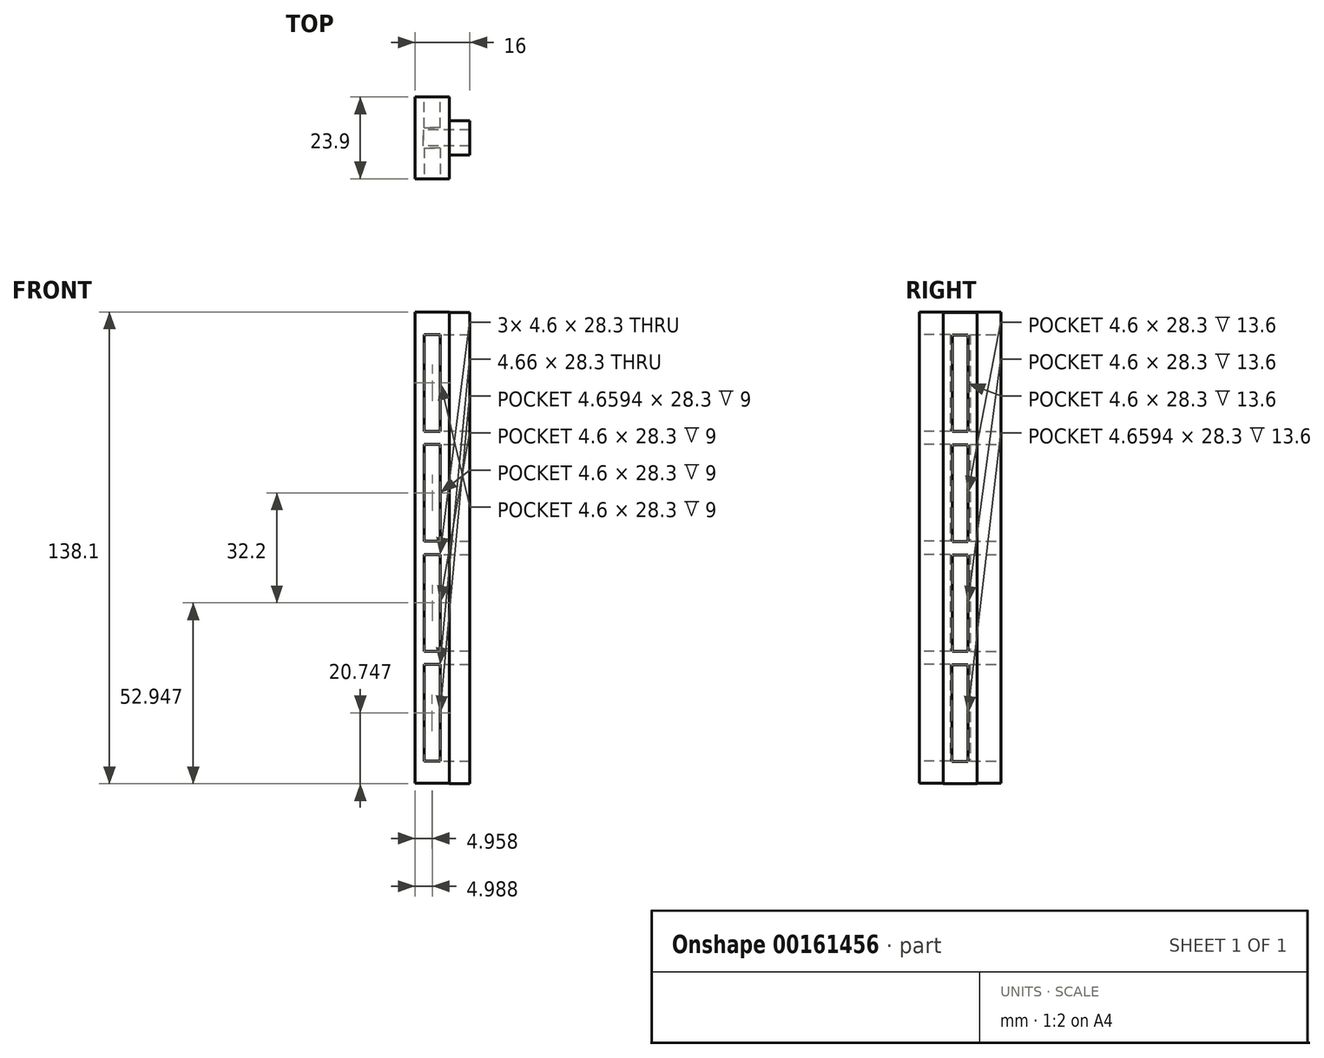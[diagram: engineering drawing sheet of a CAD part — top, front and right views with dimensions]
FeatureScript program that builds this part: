
annotation { "Feature Type Name" : "Feature", "Feature Type Description" : "" }
export const myFeature = defineFeature(function(context is Context, id is Id, definition is map)
    precondition{}
    {
        {
            var Q0;
            Q0=qCreatedBy(makeId("Front.planeOp"),FACE);
            var sketch = newSketch(context, id + "F0", { "sketchPlane" : qUnion([Q0])});
            skLineSegment(sketch, "E0.bottom", {"start": v(-30.25, 56.68) * mm, "end": v(-20.25, 56.68) * mm});
            skLineSegment(sketch, "E0.top", {"start": v(-30.25, -81.32) * mm, "end": v(-20.25, -81.32) * mm});
            skLineSegment(sketch, "E0.left", {"start": v(-30.25, 56.68) * mm, "end": v(-30.25, -81.32) * mm});
            skLineSegment(sketch, "E0.right", {"start": v(-20.25, 56.68) * mm, "end": v(-20.25, -81.32) * mm});
            skLineSegment(sketch, "E1.bottom", {"start": v(-27.56, 50.08) * mm, "end": v(-22.96, 50.08) * mm});
            skLineSegment(sketch, "E1.top", {"start": v(-27.56, 21.78) * mm, "end": v(-22.96, 21.78) * mm});
            skLineSegment(sketch, "E1.left", {"start": v(-27.56, 50.08) * mm, "end": v(-27.56, 21.78) * mm});
            skLineSegment(sketch, "E1.right", {"start": v(-22.96, 50.08) * mm, "end": v(-22.96, 21.78) * mm});
            skLineSegment(sketch, "E2", {"start": v(-26.53, 56.68) * mm, "end": v(-26.53, 50.08) * mm, "construction": true});
            skLineSegment(sketch, "E3", {"start": v(-27.56, 45.9) * mm, "end": v(-30.25, 45.9) * mm, "construction": true});
            skLineSegment(sketch, "E4", {"start": v(-22.96, 46.31) * mm, "end": v(-20.25, 46.31) * mm, "construction": true});
            skLineSegment(sketch, "E5", {"start": v(-25.26, 21.78) * mm, "end": v(-25.26, 17.88) * mm, "construction": true});
            skLineSegment(sketch, "E6", {"start": v(-27.56, 21.78) * mm, "end": v(-27.56, 17.88) * mm, "construction": true});
            skLineSegment(sketch, "E7", {"start": v(-22.96, 21.78) * mm, "end": v(-22.96, 17.88) * mm, "construction": true});
            skLineSegment(sketch, "E8.bottom", {"start": v(-27.56, 17.88) * mm, "end": v(-22.96, 17.88) * mm});
            skLineSegment(sketch, "E8.top", {"start": v(-27.56, -10.42) * mm, "end": v(-22.96, -10.42) * mm});
            skLineSegment(sketch, "E8.left", {"start": v(-27.56, 17.88) * mm, "end": v(-27.56, -10.42) * mm});
            skLineSegment(sketch, "E8.right", {"start": v(-22.96, 17.88) * mm, "end": v(-22.96, -10.42) * mm});
            skLineSegment(sketch, "E9", {"start": v(-22.96, -10.42) * mm, "end": v(-22.96, -14.32) * mm, "construction": true});
            skLineSegment(sketch, "E10", {"start": v(-27.56, -10.42) * mm, "end": v(-27.56, -14.32) * mm, "construction": true});
            skLineSegment(sketch, "E11.bottom", {"start": v(-27.56, -14.32) * mm, "end": v(-22.96, -14.32) * mm});
            skLineSegment(sketch, "E11.top", {"start": v(-27.56, -42.62) * mm, "end": v(-22.96, -42.62) * mm});
            skLineSegment(sketch, "E11.left", {"start": v(-27.56, -14.32) * mm, "end": v(-27.56, -42.62) * mm});
            skLineSegment(sketch, "E11.right", {"start": v(-22.96, -14.32) * mm, "end": v(-22.96, -42.62) * mm});
            skLineSegment(sketch, "E12", {"start": v(-27.56, -41.18) * mm, "end": v(-27.56, -42.62) * mm});
            skLineSegment(sketch, "E13", {"start": v(-22.96, -42.62) * mm, "end": v(-22.96, -46.52) * mm, "construction": true});
            skLineSegment(sketch, "E14.bottom", {"start": v(-22.96, -46.52) * mm, "end": v(-27.62, -46.52) * mm});
            skLineSegment(sketch, "E14.top", {"start": v(-22.96, -74.82) * mm, "end": v(-27.62, -74.82) * mm});
            skLineSegment(sketch, "E14.left", {"start": v(-22.96, -46.52) * mm, "end": v(-22.96, -74.82) * mm});
            skLineSegment(sketch, "E14.right", {"start": v(-27.62, -46.52) * mm, "end": v(-27.62, -74.82) * mm});
            skLineSegment(sketch, "E15", {"start": v(-22.96, -74.82) * mm, "end": v(-22.96, -81.32) * mm, "construction": true});
            skSolve(sketch);
        }
        {
            var Q0;
            Q0=makeQuery(id+"F0.imprint","IMPRINT",FACE,{"disambiguationData":[TD([[makeQuery(id+"F0.imprint","IMPRINT",EDGE,{"derivedFrom":sQuery(id+"F0.wireOp",EDGE,"E0.bottom")}),-1.0]])]});
            var Q1;
            Q1=makeQuery(id+"F0.imprint","IMPRINT",FACE,{"disambiguationData":[TD([[makeQuery(id+"F0.imprint","IMPRINT",EDGE,{"derivedFrom":sQuery(id+"F0.wireOp",EDGE,"E1.bottom")}),-1.0]])]});
            var Q2;
            Q2=makeQuery(id+"F0.imprint","IMPRINT",FACE,{"disambiguationData":[TD([[makeQuery(id+"F0.imprint","IMPRINT",EDGE,{"derivedFrom":sQuery(id+"F0.wireOp",EDGE,"E8.bottom")}),-1.0]])]});
            var Q3;
            Q3=makeQuery(id+"F0.imprint","IMPRINT",FACE,{"disambiguationData":[TD([[makeQuery(id+"F0.imprint","IMPRINT",EDGE,{"derivedFrom":sQuery(id+"F0.wireOp",EDGE,"E11.bottom")}),-1.0]])]});
            var Q4;
            Q4=makeQuery(id+"F0.imprint","IMPRINT",FACE,{"disambiguationData":[TD([[makeQuery(id+"F0.imprint","IMPRINT",EDGE,{"derivedFrom":sQuery(id+"F0.wireOp",EDGE,"E14.bottom")}),1.0]])]});
            extrude(context, id + "F1", {"entities" : qUnion([Q0, Q1, Q2, Q3, Q4]), "depth" : 11.95 * mm});
        }
        {
            var Q0;
            Q0=makeQuery(id+"F0.imprint","IMPRINT",FACE,{"disambiguationData":[TD([[makeQuery(id+"F0.imprint","IMPRINT",EDGE,{"derivedFrom":sQuery(id+"F0.wireOp",EDGE,"E1.bottom")}),-1.0]])]});
            var Q1;
            Q1=makeQuery(id+"F0.imprint","IMPRINT",FACE,{"disambiguationData":[TD([[makeQuery(id+"F0.imprint","IMPRINT",EDGE,{"derivedFrom":sQuery(id+"F0.wireOp",EDGE,"E8.bottom")}),-1.0]])]});
            var Q2;
            Q2=makeQuery(id+"F0.imprint","IMPRINT",FACE,{"disambiguationData":[TD([[makeQuery(id+"F0.imprint","IMPRINT",EDGE,{"derivedFrom":sQuery(id+"F0.wireOp",EDGE,"E11.bottom")}),-1.0]])]});
            var Q3;
            Q3=makeQuery(id+"F0.imprint","IMPRINT",FACE,{"disambiguationData":[TD([[makeQuery(id+"F0.imprint","IMPRINT",EDGE,{"derivedFrom":sQuery(id+"F0.wireOp",EDGE,"E14.bottom")}),1.0]])]});
            extrude(context, id + "F2", {"entities" : qUnion([Q0, Q1, Q2, Q3]), "operationType" : NewBodyOperationType.REMOVE, "depth" : 9 * mm});
        }
        {
            var Q0;
            Q0=makeQuery(id+"F1.opExtrude","SWEPT_BODY",BODY,{"disambiguationData":[OSD([sQuery(id+"F0.wireOp",EDGE,"E0.bottom"),sQuery(id+"F0.wireOp",EDGE,"E0.top"),sQuery(id+"F0.wireOp",EDGE,"E0.left"),sQuery(id+"F0.wireOp",EDGE,"E0.right")])]});
            var Q1;
            Q1=makeQuery(id+"F1.opExtrude","CAP_FACE",FACE,{"disambiguationData":[OSD([sQuery(id+"F0.wireOp",EDGE,"E0.bottom"),sQuery(id+"F0.wireOp",EDGE,"E0.top"),sQuery(id+"F0.wireOp",EDGE,"E0.left"),sQuery(id+"F0.wireOp",EDGE,"E0.right")])],"isStart":false});
            mirror(context, id + "F3", {"operationType" : NewBodyOperationType.ADD, "entities" : qUnion([Q0]), "mirrorPlane" : qUnion([Q1])});
        }
        {
            var Q0;
            {var subQ0=makeQuery(id+"F1.opExtrude","SWEPT_FACE",FACE,{"disambiguationData":[OSD([sQuery(id+"F0.wireOp",EDGE,"E0.right")])]});Q0=makeQuery(id+"F3.boolean.opBoolean","MERGE",FACE,{"derivedFrom":[subQ0,makeQuery(id+"F3.opPattern","COPY",FACE,{"derivedFrom":subQ0,"instanceName":"1"})]});}
            var sketch = newSketch(context, id + "F4", { "sketchPlane" : qUnion([Q0])});
            skLineSegment(sketch, "E16.bottom", {"start": v(-16.93, 56.58) * mm, "end": v(-6.93, 56.58) * mm});
            skLineSegment(sketch, "E16.top", {"start": v(-16.93, -81.42) * mm, "end": v(-6.93, -81.42) * mm});
            skLineSegment(sketch, "E16.left", {"start": v(-16.93, 56.58) * mm, "end": v(-16.93, -81.42) * mm});
            skLineSegment(sketch, "E16.right", {"start": v(-6.93, 56.58) * mm, "end": v(-6.93, -81.42) * mm});
            skLineSegment(sketch, "E17.bottom", {"start": v(-14.23, 49.98) * mm, "end": v(-9.63, 49.98) * mm});
            skLineSegment(sketch, "E17.top", {"start": v(-14.23, 21.68) * mm, "end": v(-9.63, 21.68) * mm});
            skLineSegment(sketch, "E17.left", {"start": v(-14.23, 49.98) * mm, "end": v(-14.23, 21.68) * mm});
            skLineSegment(sketch, "E17.right", {"start": v(-9.63, 49.98) * mm, "end": v(-9.63, 21.68) * mm});
            skLineSegment(sketch, "E18", {"start": v(-13.2, 56.58) * mm, "end": v(-13.2, 49.98) * mm, "construction": true});
            skLineSegment(sketch, "E19", {"start": v(-14.23, 45.8) * mm, "end": v(-16.93, 45.8) * mm, "construction": true});
            skLineSegment(sketch, "E20", {"start": v(-9.63, 46.2) * mm, "end": v(-6.93, 46.2) * mm, "construction": true});
            skLineSegment(sketch, "E21", {"start": v(-11.93, 21.68) * mm, "end": v(-11.93, 17.78) * mm, "construction": true});
            skLineSegment(sketch, "E22", {"start": v(-14.23, 21.68) * mm, "end": v(-14.23, 17.78) * mm, "construction": true});
            skLineSegment(sketch, "E23", {"start": v(-9.63, 21.68) * mm, "end": v(-9.63, 17.78) * mm, "construction": true});
            skLineSegment(sketch, "E24.bottom", {"start": v(-14.23, 17.78) * mm, "end": v(-9.63, 17.78) * mm});
            skLineSegment(sketch, "E24.top", {"start": v(-14.23, -10.52) * mm, "end": v(-9.63, -10.52) * mm});
            skLineSegment(sketch, "E24.left", {"start": v(-14.23, 17.78) * mm, "end": v(-14.23, -10.52) * mm});
            skLineSegment(sketch, "E24.right", {"start": v(-9.63, 17.78) * mm, "end": v(-9.63, -10.52) * mm});
            skLineSegment(sketch, "E25", {"start": v(-9.63, -10.52) * mm, "end": v(-9.63, -14.42) * mm, "construction": true});
            skLineSegment(sketch, "E26", {"start": v(-14.23, -10.52) * mm, "end": v(-14.23, -14.42) * mm, "construction": true});
            skLineSegment(sketch, "E27.bottom", {"start": v(-14.23, -14.42) * mm, "end": v(-9.63, -14.42) * mm});
            skLineSegment(sketch, "E27.top", {"start": v(-14.23, -42.72) * mm, "end": v(-9.63, -42.72) * mm});
            skLineSegment(sketch, "E27.left", {"start": v(-14.23, -14.42) * mm, "end": v(-14.23, -42.72) * mm});
            skLineSegment(sketch, "E27.right", {"start": v(-9.63, -14.42) * mm, "end": v(-9.63, -42.72) * mm});
            skLineSegment(sketch, "E28", {"start": v(-14.23, 18.57) * mm, "end": v(-14.23, -42.72) * mm});
            skLineSegment(sketch, "E29", {"start": v(-9.63, -42.72) * mm, "end": v(-9.63, -46.62) * mm, "construction": true});
            skLineSegment(sketch, "E30.bottom", {"start": v(-9.63, -46.62) * mm, "end": v(-14.3, -46.62) * mm});
            skLineSegment(sketch, "E30.top", {"start": v(-9.63, -74.92) * mm, "end": v(-14.3, -74.92) * mm});
            skLineSegment(sketch, "E30.left", {"start": v(-9.63, -46.62) * mm, "end": v(-9.63, -74.92) * mm});
            skLineSegment(sketch, "E30.right", {"start": v(-14.3, -46.62) * mm, "end": v(-14.3, -74.92) * mm});
            skLineSegment(sketch, "E31", {"start": v(-9.63, -74.92) * mm, "end": v(-9.63, -81.42) * mm, "construction": true});
            skSolve(sketch);
        }
        {
            var Q0;
            Q0=qSketchRegion(id+"F4",true);
            extrude(context, id + "F5", {"entities" : qUnion([Q0]), "operationType" : NewBodyOperationType.ADD, "depth" : 6 * mm});
        }
        {
            var Q0;
            {var subQ0=makeQuery(id+"F1.opExtrude","SWEPT_FACE",FACE,{"disambiguationData":[OSD([sQuery(id+"F0.wireOp",EDGE,"E0.right")])]});Q0=makeQuery(id+"F5.boolean.opBoolean","SPLIT",FACE,{"disambiguationData":[TD([makeQuery(id+"F5.opExtrude","SWEPT_FACE",FACE,{"disambiguationData":[OSD([sQuery(id+"F4.wireOp",EDGE,"E17.bottom")])]})])],"derivedFrom":makeQuery(id+"F3.boolean.opBoolean","MERGE",FACE,{"derivedFrom":[subQ0,makeQuery(id+"F3.opPattern","COPY",FACE,{"derivedFrom":subQ0,"instanceName":"1"})]})});}
            var Q1;
            {var subQ0=sQuery(id+"F4.wireOp",EDGE,"E24.bottom");var subQ3=makeQuery(id+"F1.opExtrude","SWEPT_FACE",FACE,{"disambiguationData":[OSD([sQuery(id+"F0.wireOp",EDGE,"E0.right")])]});Q1=makeQuery(id+"F5.boolean.opBoolean","SPLIT",FACE,{"disambiguationData":[TD([makeQuery(id+"F5.opExtrude","SWEPT_FACE",FACE,{"disambiguationData":[OSD([subQ0])]})])],"derivedFrom":makeQuery(id+"F3.boolean.opBoolean","MERGE",FACE,{"derivedFrom":[subQ3,makeQuery(id+"F3.opPattern","COPY",FACE,{"derivedFrom":subQ3,"instanceName":"1"})]})});}
            var Q2;
            {var subQ0=sQuery(id+"F4.wireOp",EDGE,"E27.bottom");var subQ3=makeQuery(id+"F1.opExtrude","SWEPT_FACE",FACE,{"disambiguationData":[OSD([sQuery(id+"F0.wireOp",EDGE,"E0.right")])]});Q2=makeQuery(id+"F5.boolean.opBoolean","SPLIT",FACE,{"disambiguationData":[TD([makeQuery(id+"F5.opExtrude","SWEPT_FACE",FACE,{"disambiguationData":[OSD([subQ0])]})])],"derivedFrom":makeQuery(id+"F3.boolean.opBoolean","MERGE",FACE,{"derivedFrom":[subQ3,makeQuery(id+"F3.opPattern","COPY",FACE,{"derivedFrom":subQ3,"instanceName":"1"})]})});}
            var Q3;
            {var subQ0=makeQuery(id+"F1.opExtrude","SWEPT_FACE",FACE,{"disambiguationData":[OSD([sQuery(id+"F0.wireOp",EDGE,"E0.right")])]});Q3=makeQuery(id+"F5.boolean.opBoolean","SPLIT",FACE,{"disambiguationData":[TD([makeQuery(id+"F5.opExtrude","SWEPT_FACE",FACE,{"disambiguationData":[OSD([sQuery(id+"F4.wireOp",EDGE,"E30.bottom")])]})])],"derivedFrom":makeQuery(id+"F3.boolean.opBoolean","MERGE",FACE,{"derivedFrom":[subQ0,makeQuery(id+"F3.opPattern","COPY",FACE,{"derivedFrom":subQ0,"instanceName":"1"})]})});}
            extrude(context, id + "F6", {"entities" : qUnion([Q0, Q1, Q2, Q3]), "operationType" : NewBodyOperationType.REMOVE, "oppositeDirection" : true, "depth" : 7.6 * mm});
        }
    });
